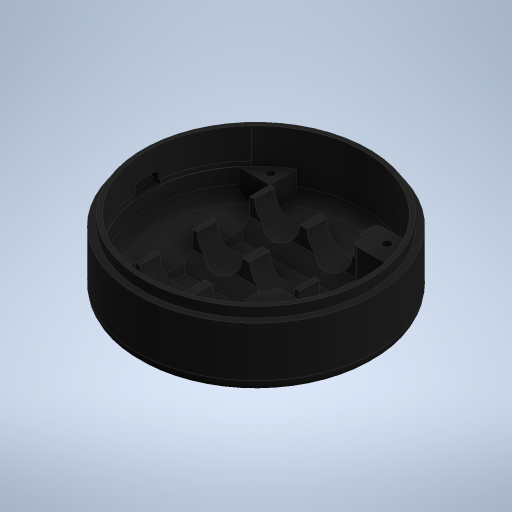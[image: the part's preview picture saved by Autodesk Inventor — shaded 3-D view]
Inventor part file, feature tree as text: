
AUTODESK INVENTOR PART (.ipt)
format: ipt  version: 2024 (Build 280153000, 153)  size: 686,592 bytes
history: native  units: mm
features: extrude x20, sketch x19, projected_geometry x14, chamfer x4, fillet x3, other x1
ambient origin geometry x8: Origin, YZ Plane, XZ Plane, XY Plane, X Axis, Y Axis, Z Axis, Center Point
bodies: Solide1 (feature_tree)
feature tree (61):
  sketch  "Esquisse1"
  extrude  "Extrusion1"  Depth=90.62mm
  extrude  "Extrusion4"  Depth=2.58mm
  fillet  "Congé2"  Radius=20.0mm
  sketch  "Esquisse6"
  sketch  "Esquisse7"
  extrude  "Extrusion5"  Depth=18.0mm
  extrude  "Extrusion6"  Depth=5.0mm TaperAngle=0.0deg
  other  "Plan de construction1"
  extrude  "Extrusion7"  Depth=5.0mm
  extrude  "Extrusion8"  Depth=90.31mm
  sketch  "Esquisse10"
  extrude  "Extrusion9"  Depth=87.0mm
  extrude  "Extrusion10"  Depth=5.0mm TaperAngle=0.0deg
  extrude  "Extrusion11"  Depth=4.0mm TaperAngle=0.0deg
  extrude  "Extrusion12"  Depth=43.0mm
  extrude  "Extrusion13"  Depth=8.0mm
  extrude  "Extrusion14"  Depth=43.0mm
  extrude  "Extrusion15"  Depth=43.0mm
  extrude  "Extrusion16"  Depth=15.0mm
  extrude  "Extrusion17"  Depth=10.0mm TaperAngle=0.0deg
  sketch  "Esquisse19"
  extrude  "Extrusion18"  Depth=18.1mm
  extrude  "Extrusion19"  Depth=18.1mm
  fillet  "Congé5"  Radius=21.1mm
  chamfer  "Chanfrein2"  Distance=10.95mm
  chamfer  "Chanfrein3"  Distance=10.0mm
  extrude  "Extrusion20"  Depth=15.3mm
  chamfer  "Chanfrein4"  Distance=21.3mm
  extrude  "Extrusion21"  Depth=12.5mm
  chamfer  "Chanfrein5"  Distance=20.0mm
  extrude  "Extrusion22"  Depth=5.0mm TaperAngle=0.0deg
  fillet  "Congé6"  Radius=10.0mm
  sketch  "Esquisse23"
  sketch  "Esquisse4"
  projected_geometry  "Boucle projetée3"
  projected_geometry  "Boucle projetée4"
  sketch  "Esquisse8"
  sketch  "Esquisse9"
  projected_geometry  "Boucle projetée5"
  sketch  "Esquisse11"
  projected_geometry  "Boucle projetée6"
  sketch  "Esquisse12"
  projected_geometry  "Boucle projetée7"
  sketch  "Esquisse13"
  projected_geometry  "Boucle projetée8"
  sketch  "Esquisse14"
  projected_geometry  "Boucle projetée9"
  sketch  "Esquisse15"
  sketch  "Esquisse16"
  projected_geometry  "Boucle projetée10"
  projected_geometry  "Boucle projetée11"
  sketch  "Esquisse18"
  projected_geometry  "Boucle projetée13"
  projected_geometry  "Boucle projetée14"
  sketch  "Esquisse20"
  sketch  "Esquisse21"
  projected_geometry  "Boucle projetée15"
  sketch  "Esquisse22"
  projected_geometry  "Boucle projetée16"
  projected_geometry  "Boucle projetée17"
